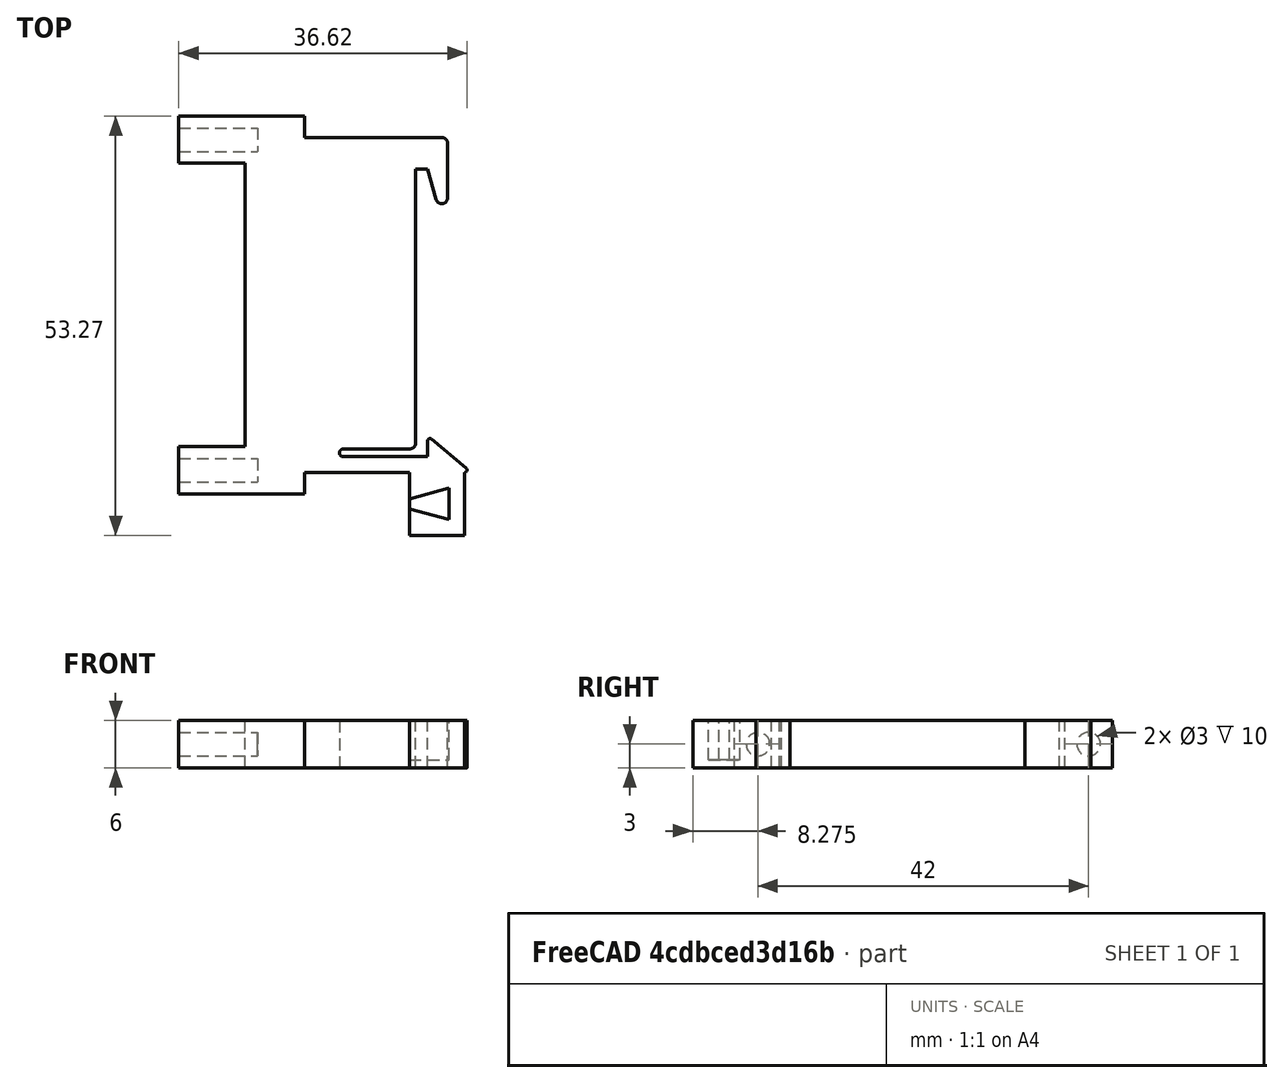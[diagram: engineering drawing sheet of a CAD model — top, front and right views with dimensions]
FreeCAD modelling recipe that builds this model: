
FCSTD DOCUMENT  (FreeCAD 0.18R4 (GitTag))
Label: orangepi-DIN-2
License: All rights reserved
LicenseURL: http://en.wikipedia.org/wiki/All_rights_reserved
objects: Sketcher::SketchObject×2, Part::Extrusion×2, Part::Cylinder×2, Part::MultiFuse×2, Part::Cut×1, Mesh::Feature×1
note: 9 computed .brp shape members not serialized (recipe doc carries the construction recipe); baked Part::Feature solids carry a one-line shape summary decoded from their .brp

FEATURE [Sketcher::SketchObject] Sketch  label="clipA-sketch"
  sketch-geometry (40):
    g0: LineSegment StartX=-16.5956 StartY=-17.875 StartZ=0 EndX=-16.5956 EndY=-23.875 EndZ=0
    g1: LineSegment StartX=-8.15558 StartY=-17.875 StartZ=0 EndX=-16.5956 EndY=-17.875 EndZ=0
    g2: LineSegment StartX=-16.5956 StartY=-23.875 StartZ=0 EndX=-0.595579 EndY=-23.875 EndZ=0
    g3: LineSegment StartX=-0.595579 StartY=-23.875 StartZ=0 EndX=-0.595579 EndY=-21.15 EndZ=0
    g4: LineSegment StartX=19.9074 StartY=-20.6005 StartZ=0 EndX=15.5111 EndY=-16.9116 EndZ=0
    g5: LineSegment StartX=15 StartY=-17.15 StartZ=0 EndX=15 EndY=-19.15 EndZ=0
    g6: LineSegment StartX=15 StartY=-19.15 StartZ=0 EndX=4.31 EndY=-19.15 EndZ=0
    g7: LineSegment StartX=4.31 StartY=-18.15 StartZ=0 EndX=12.75 EndY=-18.15 EndZ=0
    g8: LineSegment StartX=13.5 StartY=-17.4 StartZ=0 EndX=13.5 EndY=17.4 EndZ=0
    g9: LineSegment StartX=13.5 StartY=17.4 StartZ=0 EndX=15 EndY=17.4 EndZ=0
    g10: LineSegment StartX=15 StartY=17.4 StartZ=0 EndX=16.0824 EndY=13.5492 EndZ=0
    g11: LineSegment StartX=17.5544 StartY=13.7522 StartZ=0 EndX=17.5544 EndY=20.65 EndZ=0
    g12: LineSegment StartX=16.8044 StartY=21.4 StartZ=0 EndX=-0.595579 EndY=21.4 EndZ=0
    g13: LineSegment StartX=-0.595579 StartY=21.4 StartZ=0 EndX=-0.595579 EndY=24.125 EndZ=0
    g14: LineSegment StartX=-0.595579 StartY=24.125 StartZ=0 EndX=-16.5956 EndY=24.125 EndZ=0
    g15: LineSegment StartX=-16.5956 StartY=24.125 StartZ=0 EndX=-16.5956 EndY=18.125 EndZ=0
    g16: LineSegment StartX=-16.5956 StartY=18.125 StartZ=0 EndX=-8.15558 EndY=18.125 EndZ=0
    g17: LineSegment StartX=-8.15558 StartY=18.125 StartZ=0 EndX=-8.15558 EndY=-17.875 EndZ=0
    g18: ArcOfCircle CenterX=4.31 CenterY=-18.65 CenterZ=0 NormalX=0 NormalY=0 NormalZ=1 AngleXU=0 Radius=0.5 StartAngle=1.5708 EndAngle=4.71239
    g19: ArcOfCircle CenterX=19.7074 CenterY=-20.8389 CenterZ=0 NormalX=0 NormalY=0 NormalZ=1 AngleXU=0 Radius=0.311145 StartAngle=4.71239 EndAngle=7.15585
    g20: ArcOfCircle CenterX=15.3111 CenterY=-17.15 CenterZ=0 NormalX=0 NormalY=0 NormalZ=1 AngleXU=0 Radius=0.311145 StartAngle=0.872665 EndAngle=3.14159
    g21: ArcOfCircle CenterX=12.75 CenterY=-17.4 CenterZ=0 NormalX=0 NormalY=0 NormalZ=1 AngleXU=0 Radius=0.75 StartAngle=4.71239 EndAngle=6.28319
    g22: ArcOfCircle CenterX=16.8044 CenterY=13.7522 CenterZ=0 NormalX=0 NormalY=0 NormalZ=1 AngleXU=0 Radius=0.75 StartAngle=3.41561 EndAngle=6.28319
    g23: ArcOfCircle CenterX=16.8044 CenterY=20.65 CenterZ=0 NormalX=0 NormalY=0 NormalZ=1 AngleXU=0 Radius=0.75 StartAngle=1.4e-15 EndAngle=1.5708
    g24: LineSegment [constr] StartX=-8.15558 StartY=18.125 StartZ=0 EndX=-0.595579 EndY=18.125 EndZ=0
    g25: LineSegment [constr] StartX=0 StartY=0 StartZ=0 EndX=13.5 EndY=0 EndZ=0
    g26: GeomPoint X=-16.5956 Y=-20.875 Z=0
    g27: GeomPoint X=-16.5956 Y=21.125 Z=0
    g28: LineSegment [constr] StartX=-16.5956 StartY=21.125 StartZ=0 EndX=-16.5956 EndY=-20.875 EndZ=0
    g29: LineSegment StartX=12.7074 StartY=-21.15 StartZ=0 EndX=12.7074 EndY=-24.4897 EndZ=0
    g30: LineSegment StartX=19.7074 StartY=-29.15 StartZ=0 EndX=19.7074 EndY=-21.15 EndZ=0
    g31: LineSegment [constr] StartX=19.7074 StartY=-21.15 StartZ=0 EndX=12.7074 EndY=-21.15 EndZ=0
    g32: LineSegment StartX=19.7074 StartY=-29.15 StartZ=0 EndX=12.7074 EndY=-29.15 EndZ=0
    g33: LineSegment StartX=12.7074 StartY=-29.15 StartZ=0 EndX=12.7074 EndY=-25.8103 EndZ=0
    g34: LineSegment StartX=12.7074 StartY=-24.4897 StartZ=0 EndX=17.7074 EndY=-23.15 EndZ=0
    g35: LineSegment StartX=17.7074 StartY=-23.15 StartZ=0 EndX=17.7074 EndY=-27.15 EndZ=0
    g36: LineSegment StartX=17.7074 StartY=-27.15 StartZ=0 EndX=12.7074 EndY=-25.8103 EndZ=0
    g37: LineSegment [constr] StartX=12.7074 StartY=-24.4897 StartZ=0 EndX=12.7074 EndY=-25.8103 EndZ=0
    g38: GeomPoint X=17.7074 Y=-25.15 Z=0
    g39: LineSegment StartX=-0.595579 StartY=-21.15 StartZ=0 EndX=12.7074 EndY=-21.15 EndZ=0
  constraints (108):
    c: Vertical(g13)
    c: Vertical(g8)
    c: Vertical(g3)
    c: Vertical(g17)
    c: Vertical(g0)
    c: Vertical(g15)
    c: Horizontal(g14)
    c: Horizontal(g16)
    c: Horizontal(g1)
    c: Horizontal(g2)
    c: Horizontal(g12)
    c: Horizontal(g6)
    c: Horizontal(g7)
    c: Vertical(g5)
    c: Vertical(g18,g18)
    c: Vertical(g18,g18)
    c: DistanceY(g6,g7) = 1
    c: Coincident(g7,g18)
    c: Coincident(g18,g6)
    c: Coincident(g5,g6)
    c: Tangent(g4,g19) = -1.5708
    c: Coincident(g30,g19) = -1.5708
    c: DistanceX(g6,g6) = 10.69
    c: DistanceY(g3,g6) = 2
    c: DistanceX(g19,g4) = 0.2
    c: Tangent(g5,g20) = -1.5708
    c: Tangent(g4,g20) = -1.5708
    c: DistanceY(g5,g5) = 2
    c: DistanceX(g20,g4) = 0.2
    c: Tangent(g7,g21) = -1.5708
    c: Tangent(g8,g21) = -1.5708
    c: DistanceY(g7,g21) = 0.75
    c: DistanceX(g8,g5) = 1.5
    c: DistanceY(g7,g8) = 35.55
    c: Horizontal(g9)
    c: Vertical(g11)
    c: Angle(g9,g10) = 1.84481
    c: Coincident(g8,g9)
    c: DistanceY(g8,g12) = 4
    c: Coincident(g10,g9)
    c: DistanceX(g9,g9) = 1.5
    c: Tangent(g10,g22) = -1.5708
    c: Tangent(g11,g22) = -1.5708
    c: Distance(g10) = 4
    c: Tangent(g11,g23) = -1.5708
    c: Tangent(g12,g23) = -1.5708
    c: DistanceX(g22,g11) = 0.75
    c: Equal(g14,g2)
    c: Coincident(g16,g15)
    c: Coincident(g14,g15)
    c: Coincident(g14,g13)
    c: Coincident(g1,g0)
    c: Coincident(g1,g17)
    c: Coincident(g2,g0)
    c: Coincident(g3,g2)
    c: DistanceX(g14,g14) = 16
    c: PointOnObject(g24,g13)
    c: Horizontal(g24)
    c: Coincident(g12,g13)
    c: Horizontal(g25)
    c: DistanceX(g25,g25) = 13.5
    c: Coincident(g25,g-1)
    c: DistanceX(g23,g11) = 0.75
    c: DistanceY(g15,g15) = 6  'mntSize'
    c: Coincident(g24,g17)
    c: Coincident(g17,g16)
    c: Equal(g3,g13)
    c: Equal(g3,g13)
    c: Equal(g1,g16)
    c: Equal(g2,g14)
    c: Equal(g0,g15)
    c: DistanceX(g12,g12) = 17.4
    c: Symmetric(g0,g0,g26)
    c: Symmetric(g15,g15,g27)
    c: DistanceY(g28,g28) = 42
    c: Coincident(g26,g28)
    c: Coincident(g27,g28)
    c: DistanceX(g24,g24) = 7.56
    c: Symmetric(g8,g8,g25)
    c: Vertical(g29)
    c: Vertical(g30)
    c: Coincident(g29,g31)
    c: Coincident(g31,g30)
    c: Horizontal(g31)
    c: Horizontal(g32)
    c: Vertical(g35)
    c: Vertical(g33)
    c: Coincident(g29,g34)
    c: Coincident(g36,g33)
    c: Coincident(g32,g33)
    c: Coincident(g35,g36)
    c: Coincident(g35,g34)
    c: Vertical(g29,g33)
    c: Coincident(g37,g29)
    c: Coincident(g37,g33)
    c: Coincident(g30,g32)
    c: DistanceX(g35,g30) = 2
    c: DistanceX(g33,g35) = 5
    c: DistanceY(g30,g30) = 8
    c: Angle(g34,g35) = 1.309
    c: Angle(g35,g36) = 1.309
    c: Symmetric(g35,g35,g38)
    c: Equal(g29,g33)
    c: DistanceY(g32,g35) = 2
    c: DistanceY(g19,g5) = 2
    c: Coincident(g39,g3)
    c: Coincident(g29,g39)
    c: Angle(g5,g4) = 0.872665
FEATURE [Part::Extrusion] Extrude
  Base = -> Sketch
  Dir = (0,0,1)
  DirMode = 2
  FaceMakerClass = Part::FaceMakerBullseye
  LengthFwd = 6
  LengthRev = 0
  Solid = true
  Symmetric = false
FEATURE [Part::Cylinder] Cylinder  label="screw-A"
  Angle = 360
  AttacherType = Attacher::AttachEngine3D
  Height = 10
  MapMode = 45
  Placement = pos=(-16.5956,21.125,3) rot=(0.57735,0.57735,0.57735;2.0944rad)
  Radius = 1.5
  Support = -> [Extrude]
FEATURE [Part::Cylinder] Cylinder001  label="screw-B"
  Angle = 360
  AttacherType = Attacher::AttachEngine3D
  Height = 10
  MapMode = 45
  Placement = pos=(-16.5956,-20.875,3) rot=(0.57735,0.57735,0.57735;2.0944rad)
  Radius = 1.5
  Support = -> [Extrude]
FEATURE [Sketcher::SketchObject] Sketch001  label="openHandleSketch"
  MapMode = 2
  sketch-geometry (4):
    g0: LineSegment StartX=12.7074 StartY=-29.15 StartZ=0 EndX=19.7074 EndY=-29.15 EndZ=0
    g1: LineSegment StartX=19.7074 StartY=-29.15 StartZ=0 EndX=19.7074 EndY=-21.15 EndZ=0
    g2: LineSegment StartX=19.7074 StartY=-21.15 StartZ=0 EndX=12.7074 EndY=-21.15 EndZ=0
    g3: LineSegment StartX=12.7074 StartY=-21.15 StartZ=0 EndX=12.7074 EndY=-29.15 EndZ=0
  constraints (8):
    c: Coincident(g0,g1)
    c: Coincident(g1,g2)
    c: Coincident(g2,g3)
    c: Coincident(g3,g0)
    c: Horizontal(g0)
    c: Horizontal(g2)
    c: Vertical(g1)
    c: Vertical(g3)
FEATURE [Part::Extrusion] Extrude001  label="openHandleBottom"
  Base = -> Sketch001
  Dir = (0,0,1)
  DirMode = 2
  FaceMakerClass = Part::FaceMakerBullseye
  LengthFwd = 1
  LengthRev = 0
  Solid = true
  Symmetric = false
FEATURE [Part::MultiFuse] Fusion  label="screwHoles"
  Shapes = -> [Cylinder,Cylinder001]
FEATURE [Part::Cut] Cut
  Base = -> Extrude
  Tool = -> Fusion
FEATURE [Part::MultiFuse] Fusion001
  Shapes = -> [Extrude001,Cut]
FEATURE [Mesh::Feature] Mesh  label="Fusion001 (Meshed)"
